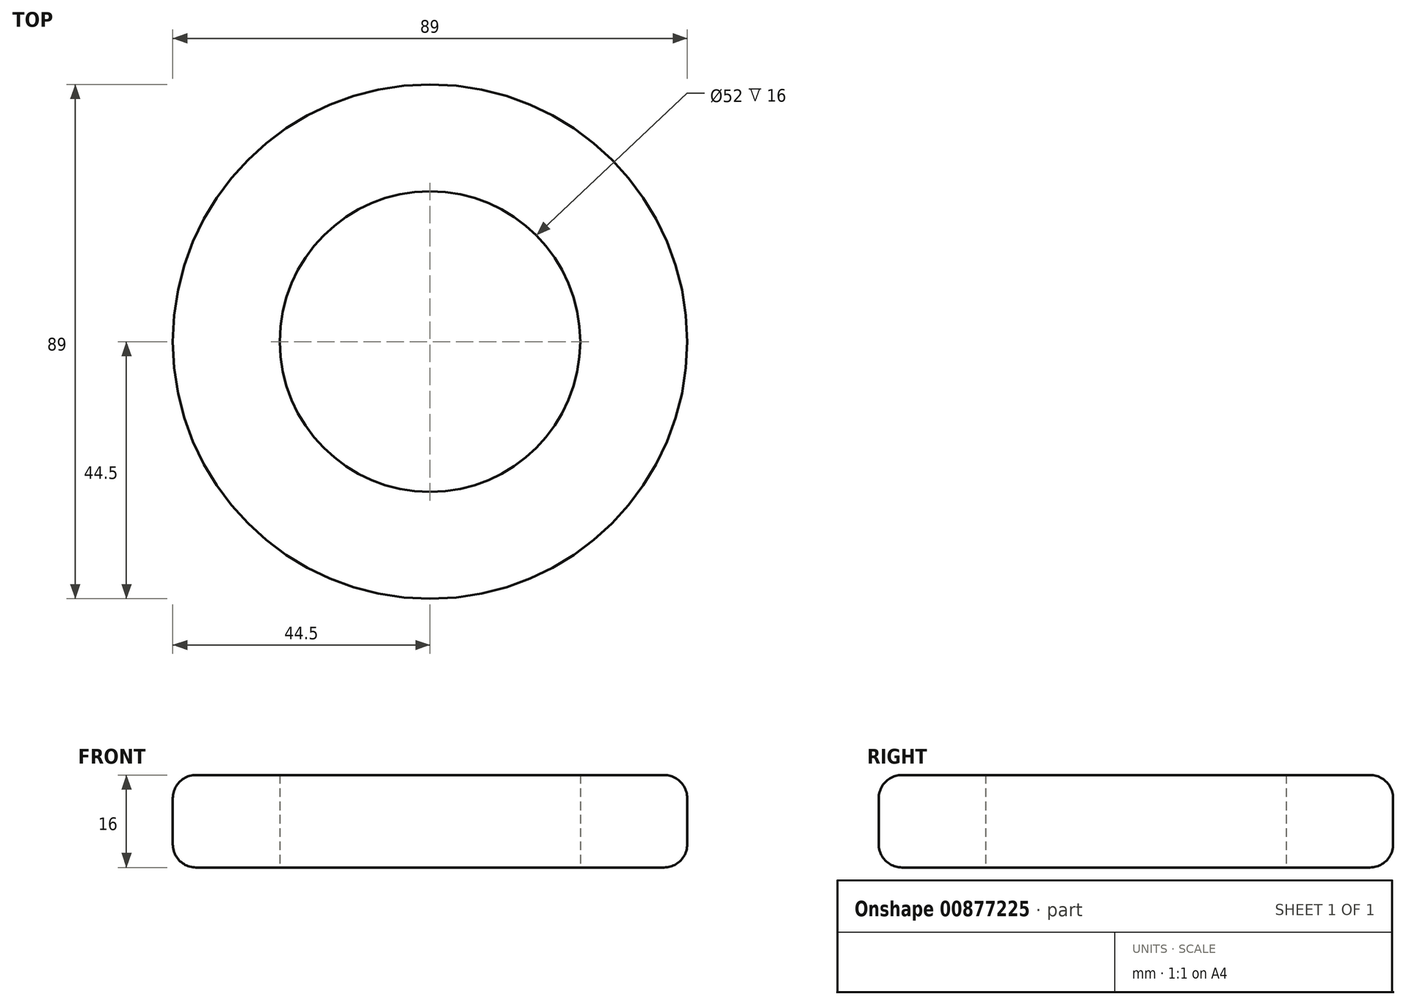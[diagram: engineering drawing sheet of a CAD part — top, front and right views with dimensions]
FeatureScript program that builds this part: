
annotation { "Feature Type Name" : "Feature", "Feature Type Description" : "" }
export const myFeature = defineFeature(function(context is Context, id is Id, definition is map)
    precondition{}
    {
        {
            var Q0;
            Q0=qCreatedBy(makeId("Top.planeOp"),FACE);
            var sketch = newSketch(context, id + "F0", { "sketchPlane" : qUnion([Q0])});
            skCircle(sketch, "E0", {"center": v(0, 0) * mm, "radius": 26 * mm});
            skCircle(sketch, "E1", {"center": v(0, 0) * mm, "radius": 44.5 * mm});
            skSolve(sketch);
        }
        {
            var Q0;
            Q0=makeQuery(id+"F0.imprint","IMPRINT",FACE,{"disambiguationData":[TD([[makeQuery(id+"F0.imprint","IMPRINT",EDGE,{"derivedFrom":sQuery(id+"F0.wireOp",EDGE,"E0")}),-1.0]])]});
            extrude(context, id + "F1", {"entities" : qUnion([Q0]), "depth" : 16 * mm, "offsetDistance" : 25 * mm});
        }
        {
            var Q0;
            Q0=makeQuery(id+"F1.opExtrude","CAP_EDGE",EDGE,{"disambiguationData":[OSD([sQuery(id+"F0.wireOp",EDGE,"E1")])],"isStart":true});
            var Q1;
            Q1=makeQuery(id+"F1.opExtrude","SWEPT_FACE",FACE,{"disambiguationData":[OSD([sQuery(id+"F0.wireOp",EDGE,"E1")])]});
            fillet(context, id + "F2", {"entities" : qUnion([Q0, Q1]), "radius" : 4 * mm, "tangentPropagation" : true, "allowEdgeOverflow" : false});
        }
    });
